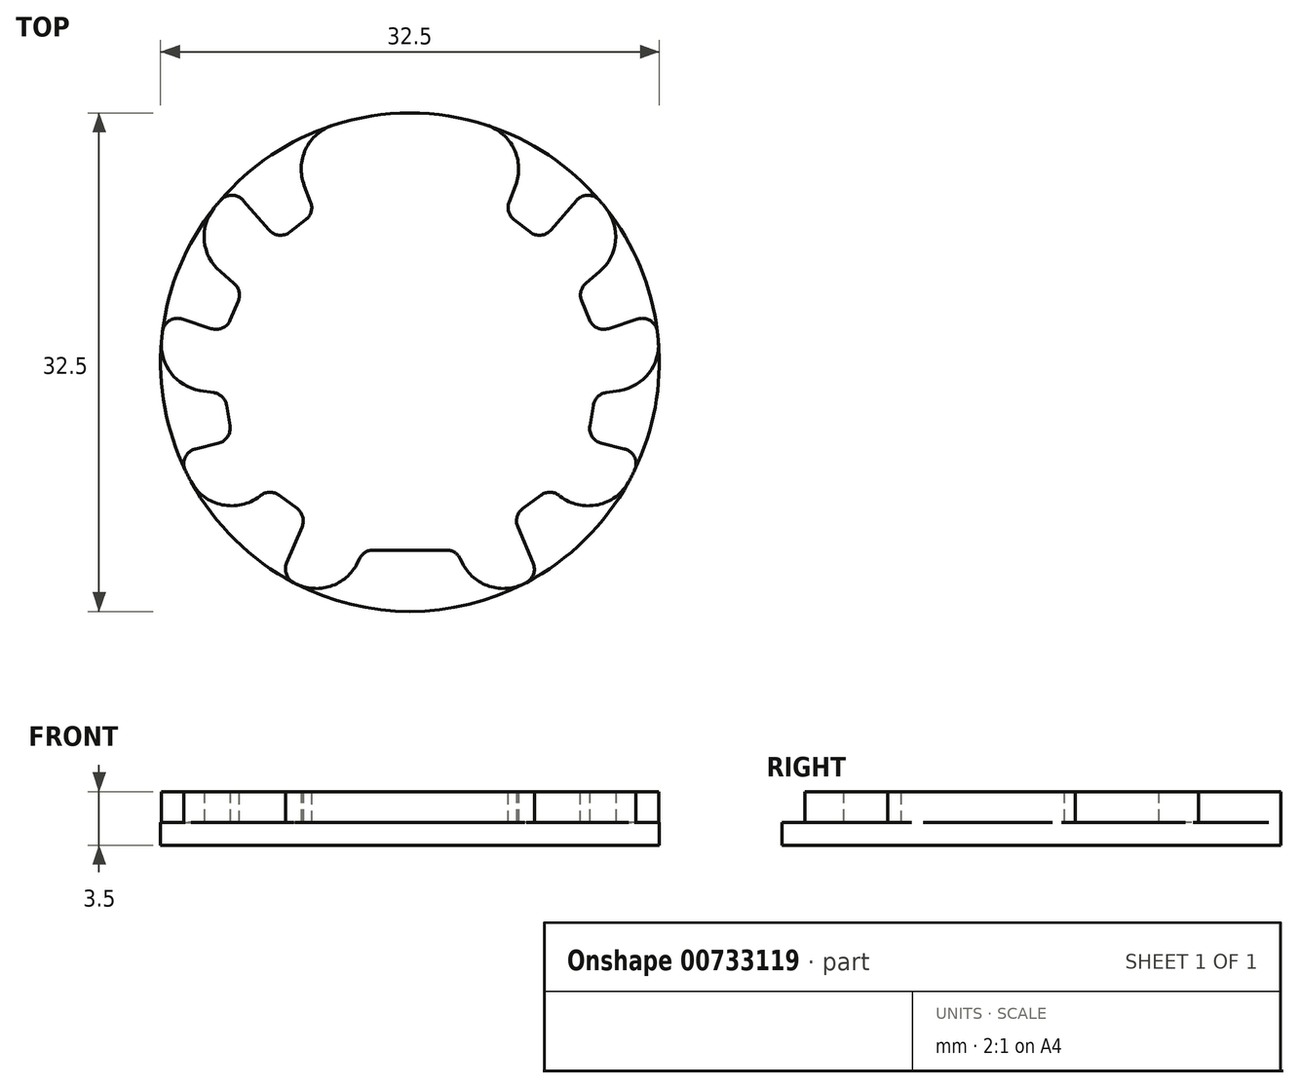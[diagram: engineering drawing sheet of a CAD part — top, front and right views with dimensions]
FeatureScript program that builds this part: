
annotation { "Feature Type Name" : "Feature", "Feature Type Description" : "" }
export const myFeature = defineFeature(function(context is Context, id is Id, definition is map)
    precondition{}
    {
        {
            var Q0;
            Q0=qCreatedBy(makeId("Top.planeOp"),FACE);
            var sketch = newSketch(context, id + "F0", { "sketchPlane" : qUnion([Q0])});
            skArc(sketch, "E0", {"start": v(0, -16.25) * mm, "mid": v(16.25, 0) * mm, "end": v(0, 16.25) * mm});
            skLineSegment(sketch, "E1", {"start": v(0, -15.75) * mm, "end": v(0, -12.25) * mm, "construction": true});
            skLineSegment(sketch, "E2", {"start": v(2.25, -12.25) * mm, "end": v(6.72, -10.01) * mm, "construction": true});
            skLineSegment(sketch, "E3", {"start": v(6.72, -10.01) * mm, "end": v(8.38, -13.92) * mm});
            skLineSegment(sketch, "E4", {"start": v(6.72, -10.01) * mm, "end": v(9.22, -13.38) * mm, "construction": true});
            skLineSegment(sketch, "E5", {"start": v(6.72, -10.01) * mm, "end": v(9.13, -8.22) * mm});
            skLineSegment(sketch, "E6", {"start": v(9.13, -8.22) * mm, "end": v(12.27, -10.65) * mm});
            skPoint(sketch, "E7", {"position": v(0, -3.1) * mm});
            skLineSegment(sketch, "E8", {"start": v(9.13, -8.22) * mm, "end": v(11.58, -5.06) * mm, "construction": true});
            skLineSegment(sketch, "E9", {"start": v(0, -3.1) * mm, "end": v(15.25, -5.61) * mm, "construction": true});
            skLineSegment(sketch, "E10", {"start": v(11.58, -5.06) * mm, "end": v(12.06, -2.1) * mm, "construction": true});
            skLineSegment(sketch, "E11", {"start": v(0, -3.1) * mm, "end": v(16.16, -1.7) * mm, "construction": true});
            skLineSegment(sketch, "E12", {"start": v(11.58, -5.06) * mm, "end": v(15.13, -5.93) * mm});
            skLineSegment(sketch, "E13", {"start": v(11.58, -5.06) * mm, "end": v(12.06, -2.1) * mm});
            skLineSegment(sketch, "E14", {"start": v(12.06, -2.1) * mm, "end": v(12.06, 1.9) * mm, "construction": true});
            skLineSegment(sketch, "E15", {"start": v(0, -3.1) * mm, "end": v(15.87, 3.48) * mm, "construction": true});
            skLineSegment(sketch, "E16", {"start": v(12.06, 1.9) * mm, "end": v(10.91, 4.67) * mm, "construction": true});
            skLineSegment(sketch, "E17", {"start": v(0, -3.1) * mm, "end": v(14.53, 7.28) * mm, "construction": true});
            skLineSegment(sketch, "E18", {"start": v(12.06, 1.9) * mm, "end": v(15.93, 3.18) * mm});
            skLineSegment(sketch, "E19", {"start": v(12.06, 1.9) * mm, "end": v(10.91, 4.67) * mm});
            skLineSegment(sketch, "E20", {"start": v(10.91, 4.67) * mm, "end": v(8.57, 7.91) * mm, "construction": true});
            skLineSegment(sketch, "E21", {"start": v(0, -3.1) * mm, "end": v(11.38, 11.6) * mm, "construction": true});
            skLineSegment(sketch, "E22", {"start": v(8.57, 7.91) * mm, "end": v(6.2, 9.75) * mm, "construction": true});
            skLineSegment(sketch, "E23", {"start": v(0, -3.1) * mm, "end": v(8.2, 14.02) * mm, "construction": true});
            skLineSegment(sketch, "E24", {"start": v(8.57, 7.91) * mm, "end": v(11.59, 11.4) * mm});
            skLineSegment(sketch, "E25", {"start": v(8.57, 7.91) * mm, "end": v(6.2, 9.75) * mm});
            skLineSegment(sketch, "E26", {"start": v(6.2, 9.75) * mm, "end": v(2.58, 11.45) * mm, "construction": true});
            skLineSegment(sketch, "E27", {"start": v(0, -3.1) * mm, "end": v(3.37, 15.9) * mm, "construction": true});
            skLineSegment(sketch, "E28", {"start": v(0, 16.25) * mm, "end": v(0, -16.25) * mm});
            skLineSegment(sketch, "E29", {"start": v(6.2, 9.75) * mm, "end": v(7.9, 14.2) * mm});
            skLineSegment(sketch, "E30", {"start": v(10.91, 4.67) * mm, "end": v(14.35, 7.62) * mm});
            skLineSegment(sketch, "E31", {"start": v(12.06, -2.1) * mm, "end": v(16.19, -1.42) * mm});
            skLineSegment(sketch, "E32", {"start": v(0, -12.25) * mm, "end": v(3, -12.25) * mm});
            skLineSegment(sketch, "E33", {"start": v(3, -12.25) * mm, "end": v(4.66, -15.57) * mm});
            skSolve(sketch);
        }
        {
            var Q0;
            Q0 = qSketchRegion(id + "F0", true);
            extrude(context, id + "F1", {"entities" : qUnion([Q0]), "depth" : 1.5 * mm, "offsetDistance" : 25 * mm});
        }
        {
            var Q0;
            {var subQ1=sQuery(id+"F0.wireOp",EDGE,"E3");Q0=makeQuery(id+"F0.imprint","IMPRINT",FACE,{"disambiguationData":[TD([[makeQuery(id+"F0.imprint","IMPRINT",EDGE,{"derivedFrom":subQ1}),-1.0]])]});}
            extrude(context, id + "F2", {"entities" : qUnion([Q0]), "operationType" : NewBodyOperationType.ADD, "depth" : 3.5 * mm, "offsetDistance" : 25 * mm});
        }
        {
            var Q0;
            Q0=makeQuery(id+"F2.opExtrude","SWEPT_EDGE",EDGE,{"disambiguationData":[OSD([sQuery(id+"F0.wireOp",EDGE,"E32"),sQuery(id+"F0.wireOp",EDGE,"E33")])]});
            var Q1;
            Q1=makeQuery(id+"F2.opExtrude","SWEPT_EDGE",EDGE,{"disambiguationData":[OSD([sQuery(id+"F0.wireOp",EDGE,"E5"),sQuery(id+"F0.wireOp",EDGE,"E6")])]});
            var Q2;
            Q2=makeQuery(id+"F2.opExtrude","SWEPT_EDGE",EDGE,{"disambiguationData":[OSD([sQuery(id+"F0.wireOp",EDGE,"E13"),sQuery(id+"F0.wireOp",EDGE,"E31")])]});
            var Q3;
            Q3=makeQuery(id+"F2.opExtrude","SWEPT_EDGE",EDGE,{"disambiguationData":[OSD([sQuery(id+"F0.wireOp",EDGE,"E19"),sQuery(id+"F0.wireOp",EDGE,"E30")])]});
            var Q4;
            Q4=makeQuery(id+"F2.opExtrude","SWEPT_EDGE",EDGE,{"disambiguationData":[OSD([sQuery(id+"F0.wireOp",EDGE,"E25"),sQuery(id+"F0.wireOp",EDGE,"E29")])]});
            fillet(context, id + "F3", {"entities" : qUnion([Q0, Q1, Q2, Q3, Q4]), "radius" : 1 * mm, "tangentPropagation" : true, "allowEdgeOverflow" : false});
        }
        {
            var Q0;
            Q0=makeQuery(id+"F2.opExtrude","SWEPT_EDGE",EDGE,{"disambiguationData":[OSD([sQuery(id+"F0.wireOp",EDGE,"E18"),sQuery(id+"F0.wireOp",EDGE,"E19")])]});
            var Q1;
            Q1=makeQuery(id+"F2.opExtrude","SWEPT_EDGE",EDGE,{"disambiguationData":[OSD([sQuery(id+"F0.wireOp",EDGE,"E12"),sQuery(id+"F0.wireOp",EDGE,"E13")])]});
            var Q2;
            Q2=makeQuery(id+"F2.opExtrude","SWEPT_EDGE",EDGE,{"disambiguationData":[OSD([sQuery(id+"F0.wireOp",EDGE,"E3"),sQuery(id+"F0.wireOp",EDGE,"E5")])]});
            var Q3;
            Q3=makeQuery(id+"F2.opExtrude","SWEPT_EDGE",EDGE,{"disambiguationData":[OSD([sQuery(id+"F0.wireOp",EDGE,"E24"),sQuery(id+"F0.wireOp",EDGE,"E25")])]});
            var Q4;
            Q4=makeQuery(id+"F2.opExtrude","SWEPT_EDGE",EDGE,{"disambiguationData":[OSD([sQuery(id+"F0.wireOp",EDGE,"2Oi86fdV-0eIK-pSgj-a3kG-A2ANFbIYnlkr"),sQuery(id+"F0.wireOp",EDGE,"hmDe4cDL-ggfA-SONU-tol5-plaIjJrWZ28Z")])]});
            fillet(context, id + "F4", {"entities" : qUnion([Q0, Q1, Q2, Q3, Q4]), "radius" : 1 * mm, "tangentPropagation" : true, "allowEdgeOverflow" : false});
        }
        {
            var Q0;
            Q0=makeQuery(id+"F2.opExtrude","SWEPT_EDGE",EDGE,{"disambiguationData":[OSD([sQuery(id+"F0.wireOp",EDGE,"E0"),sQuery(id+"F0.wireOp",EDGE,"E33")])]});
            var Q1;
            Q1=makeQuery(id+"F2.opExtrude","SWEPT_EDGE",EDGE,{"disambiguationData":[OSD([sQuery(id+"F0.wireOp",EDGE,"E0"),sQuery(id+"F0.wireOp",EDGE,"E6")])]});
            var Q2;
            Q2=makeQuery(id+"F2.opExtrude","SWEPT_EDGE",EDGE,{"disambiguationData":[OSD([sQuery(id+"F0.wireOp",EDGE,"E0"),sQuery(id+"F0.wireOp",EDGE,"E31")])]});
            var Q3;
            Q3=makeQuery(id+"F2.opExtrude","SWEPT_EDGE",EDGE,{"disambiguationData":[OSD([sQuery(id+"F0.wireOp",EDGE,"E0"),sQuery(id+"F0.wireOp",EDGE,"E30")])]});
            var Q4;
            Q4=makeQuery(id+"F2.opExtrude","SWEPT_EDGE",EDGE,{"disambiguationData":[OSD([sQuery(id+"F0.wireOp",EDGE,"E0"),sQuery(id+"F0.wireOp",EDGE,"E29")])]});
            fillet(context, id + "F5", {"entities" : qUnion([Q0, Q1, Q2, Q3, Q4]), "radius" : 3 * mm, "tangentPropagation" : true, "allowEdgeOverflow" : false});
        }
        {
            var Q0;
            Q0=makeQuery(id+"F2.opExtrude","SWEPT_EDGE",EDGE,{"disambiguationData":[OSD([sQuery(id+"F0.wireOp",EDGE,"E0"),sQuery(id+"F0.wireOp",EDGE,"E3")])]});
            var Q1;
            Q1=makeQuery(id+"F2.opExtrude","SWEPT_EDGE",EDGE,{"disambiguationData":[OSD([sQuery(id+"F0.wireOp",EDGE,"E0"),sQuery(id+"F0.wireOp",EDGE,"E12")])]});
            var Q2;
            Q2=makeQuery(id+"F2.opExtrude","SWEPT_EDGE",EDGE,{"disambiguationData":[OSD([sQuery(id+"F0.wireOp",EDGE,"E0"),sQuery(id+"F0.wireOp",EDGE,"E18")])]});
            var Q3;
            Q3=makeQuery(id+"F2.opExtrude","SWEPT_EDGE",EDGE,{"disambiguationData":[OSD([sQuery(id+"F0.wireOp",EDGE,"E0"),sQuery(id+"F0.wireOp",EDGE,"E24")])]});
            fillet(context, id + "F6", {"entities" : qUnion([Q0, Q1, Q2, Q3]), "radius" : 1 * mm, "tangentPropagation" : true, "allowEdgeOverflow" : false});
        }
        {
            var Q0;
            Q0=makeQuery(id+"F1.opExtrude","SWEPT_BODY",BODY,{"disambiguationData":[OSD([sQuery(id+"F0.wireOp",EDGE,"E0"),sQuery(id+"F0.wireOp",EDGE,"E28")])]});
            var Q1;
            {var subQ0=sQuery(id+"F0.wireOp",EDGE,"E28");Q1=makeQuery(id+"F2.boolean.opBoolean","MERGE",FACE,{"derivedFrom":[makeQuery(id+"F1.opExtrude","SWEPT_FACE",FACE,{"disambiguationData":[OSD([subQ0])]}),makeQuery(id+"F2.opExtrude","SWEPT_FACE",FACE,{"disambiguationData":[OSD([subQ0])]})]});}
            mirror(context, id + "F7", {"operationType" : NewBodyOperationType.ADD, "entities" : qUnion([Q0]), "mirrorPlane" : qUnion([Q1])});
        }
    });
